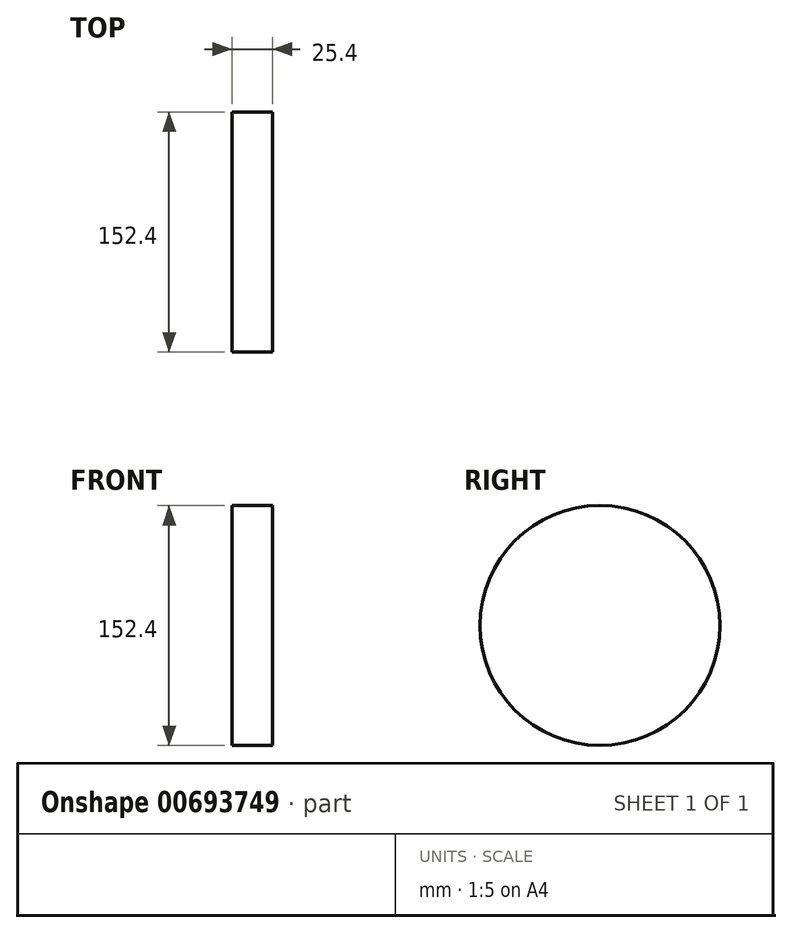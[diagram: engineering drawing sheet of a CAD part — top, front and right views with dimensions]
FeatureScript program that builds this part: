
annotation { "Feature Type Name" : "Feature", "Feature Type Description" : "" }
export const myFeature = defineFeature(function(context is Context, id is Id, definition is map)
    precondition{}
    {
        {
            var Q0;
            Q0=qCreatedBy(makeId("Right.planeOp"),FACE);
            var sketch = newSketch(context, id + "F0", { "sketchPlane" : qUnion([Q0])});
            skCircle(sketch, "E0", {"center": v(0, 0) * mm, "radius": 76.2 * mm});
            skSolve(sketch);
        }
        {
            var Q0;
            Q0=makeQuery(id+"F0.imprint","IMPRINT",FACE,{"disambiguationData":[TD([[makeQuery(id+"F0.imprint","IMPRINT",EDGE,{"derivedFrom":sQuery(id+"F0.wireOp",EDGE,"E0")}),1.0]])]});
            extrude(context, id + "F1", {"entities" : qUnion([Q0]), "depth" : 25.4 * mm, "offsetDistance" : 25.4 * mm});
        }
    });
